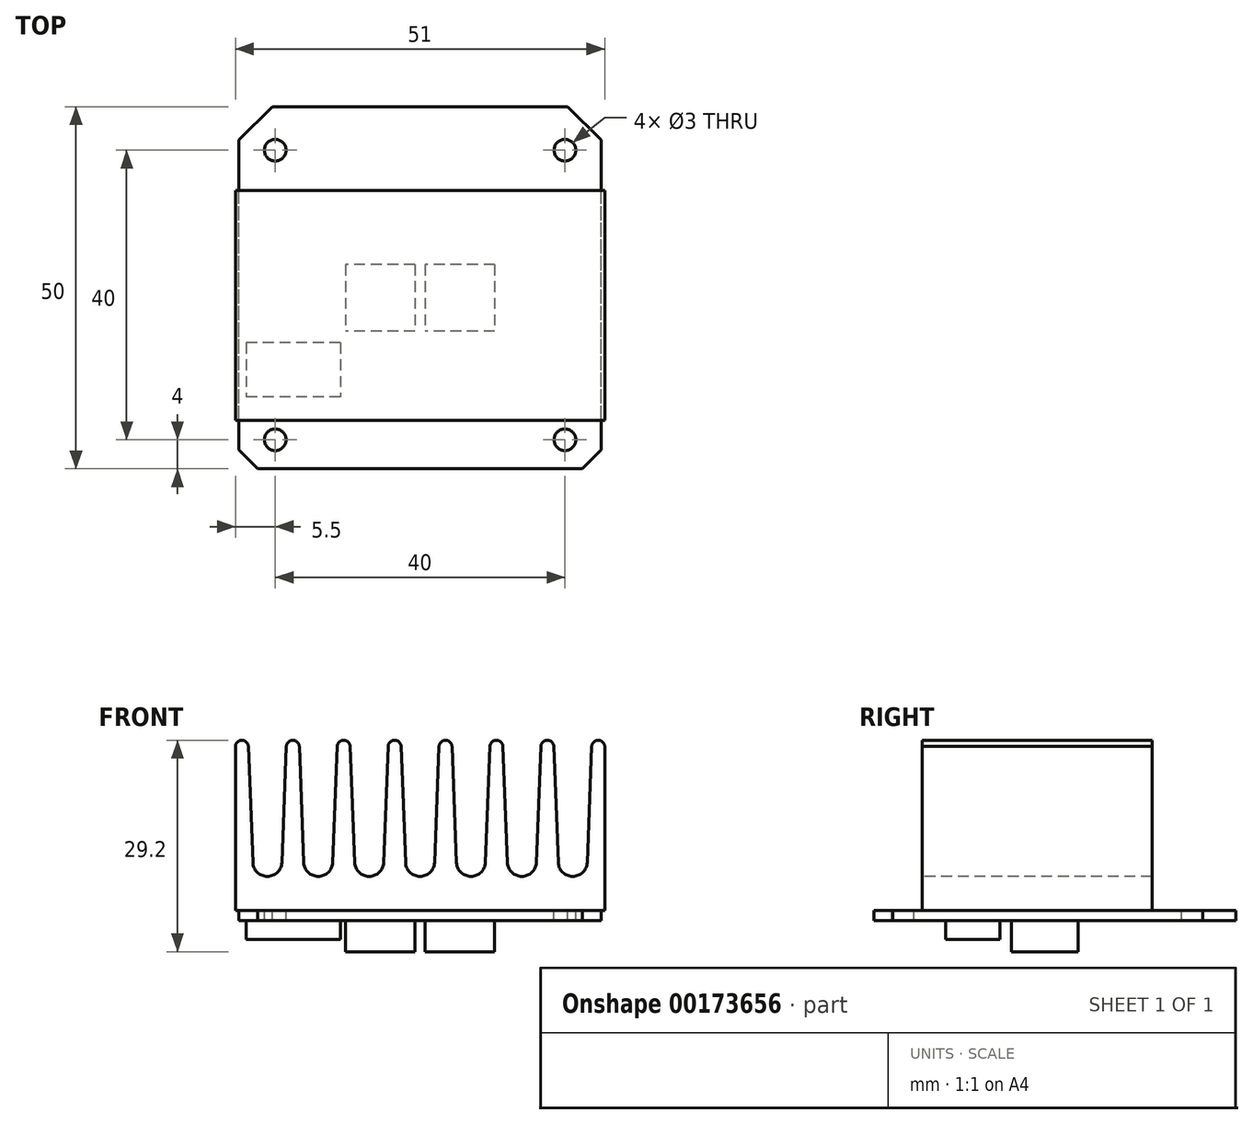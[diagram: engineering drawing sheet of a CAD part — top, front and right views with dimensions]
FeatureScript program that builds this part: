
annotation { "Feature Type Name" : "Feature", "Feature Type Description" : "" }
export const myFeature = defineFeature(function(context is Context, id is Id, definition is map)
    precondition{}
    {
        {
            var Q0;
            Q0=qCreatedBy(makeId("Top.planeOp"),FACE);
            var sketch = newSketch(context, id + "F0", { "sketchPlane" : qUnion([Q0])});
            skLineSegment(sketch, "E0.bottom", {"start": v(-25, -25) * mm, "end": v(25, -25) * mm});
            skLineSegment(sketch, "E0.top", {"start": v(-25, 25) * mm, "end": v(25, 25) * mm});
            skLineSegment(sketch, "E0.left", {"start": v(-25, -25) * mm, "end": v(-25, 25) * mm});
            skLineSegment(sketch, "E0.right", {"start": v(25, -25) * mm, "end": v(25, 25) * mm});
            skPoint(sketch, "E0.middle", {"position": v(0, 0) * mm});
            skLineSegment(sketch, "E1", {"start": v(0, 0) * mm, "end": v(0, -1) * mm, "construction": true});
            skLineSegment(sketch, "E2.bottom", {"start": v(20, 19) * mm, "end": v(-20, 19) * mm, "construction": true});
            skLineSegment(sketch, "E2.top", {"start": v(20, -21) * mm, "end": v(-20, -21) * mm, "construction": true});
            skLineSegment(sketch, "E2.left", {"start": v(20, 19) * mm, "end": v(20, -21) * mm, "construction": true});
            skLineSegment(sketch, "E2.right", {"start": v(-20, 19) * mm, "end": v(-20, -21) * mm, "construction": true});
            skPoint(sketch, "E2.middle", {"position": v(0, -1) * mm});
            skCircle(sketch, "E3", {"center": v(20, 19) * mm, "radius": 1.5 * mm});
            skCircle(sketch, "E4", {"center": v(20, -21) * mm, "radius": 1.5 * mm});
            skCircle(sketch, "E5", {"center": v(-20, -21) * mm, "radius": 1.5 * mm});
            skCircle(sketch, "E6", {"center": v(-20, 19) * mm, "radius": 1.5 * mm});
            skPoint(sketch, "E7.endSnap0", {"position": v(0, 19) * mm});
            skLineSegment(sketch, "E8", {"start": v(-12.7, 20.27) * mm, "end": v(2.54, 20.27) * mm, "construction": true});
            skPoint(sketch, "E9", {"position": v(-12.7, 20.27) * mm});
            skPoint(sketch, "E10", {"position": v(2.54, 20.27) * mm});
            skLineSegment(sketch, "E11", {"start": v(-25, -22.4) * mm, "end": v(-22.4, -25) * mm});
            skLineSegment(sketch, "E12", {"start": v(22.4, -25) * mm, "end": v(25, -22.4) * mm});
            skLineSegment(sketch, "E13", {"start": v(25, 20.4) * mm, "end": v(20.4, 25) * mm});
            skLineSegment(sketch, "E14", {"start": v(-20.4, 25) * mm, "end": v(-25, 20.4) * mm});
            skSolve(sketch);
        }
        {
            var Q0;
            Q0=makeQuery(id+"F0.imprint","IMPRINT",FACE,{"disambiguationData":[TD([[makeQuery(id+"F0.imprint","IMPRINT",EDGE,{"derivedFrom":sQuery(id+"F0.wireOp",EDGE,"E3")}),-1.0]])]});
            extrude(context, id + "F1", {"entities" : qUnion([Q0]), "oppositeDirection" : true, "depth" : 1.4 * mm});
        }
        {
            var Q0;
            Q0=makeQuery(id+"F0.imprint","IMPRINT",FACE,{"disambiguationData":[TD([[makeQuery(id+"F0.imprint","IMPRINT",EDGE,{"derivedFrom":sQuery(id+"F0.wireOp",EDGE,"E0.bottom")}),1.0]])]});
            var sketch = newSketch(context, id + "F2", { "sketchPlane" : qUnion([Q0])});
            skLineSegment(sketch, "E15.bottom", {"start": v(-25.5, 13.4) * mm, "end": v(25.5, 13.4) * mm});
            skLineSegment(sketch, "E15.top", {"start": v(-25.5, -18.3) * mm, "end": v(25.5, -18.3) * mm});
            skLineSegment(sketch, "E15.left", {"start": v(-25.5, 13.4) * mm, "end": v(-25.5, -18.3) * mm});
            skLineSegment(sketch, "E15.right", {"start": v(25.5, 13.4) * mm, "end": v(25.5, -18.3) * mm});
            skPoint(sketch, "E15.middle", {"position": v(0, -2.45) * mm});
            skSolve(sketch);
        }
        {
            var Q0;
            Q0 = qSketchRegion(id + "F2", true);
            extrude(context, id + "F3", {"entities" : qUnion([Q0]), "depth" : 23.5 * mm});
        }
        {
            var Q0;
            Q0=makeQuery(id+"F3.opExtrude","SWEPT_FACE",FACE,{"disambiguationData":[OSD([sQuery(id+"F2.wireOp",EDGE,"E15.top")])]});
            var sketch = newSketch(context, id + "F4", { "sketchPlane" : qUnion([Q0])});
            skLineSegment(sketch, "E16", {"start": v(-2.62, 22.63) * mm, "end": v(-2, 6.62) * mm});
            skArc(sketch, "E17", {"start": v(-2, 6.62) * mm, "mid": v(0, 4.7) * mm, "end": v(2, 6.62) * mm});
            skLineSegment(sketch, "E18", {"start": v(2, 6.62) * mm, "end": v(2.62, 22.63) * mm});
            skLineSegment(sketch, "E19", {"start": v(0, 23.5) * mm, "end": v(0, 6.7) * mm, "construction": true});
            skArc(sketch, "E20", {"start": v(4.41, 22.63) * mm, "mid": v(3.51, 23.5) * mm, "end": v(2.62, 22.63) * mm});
            skLineSegment(sketch, "E21.1.0.0", {"start": v(4.41, 22.63) * mm, "end": v(5.03, 6.62) * mm});
            skLineSegment(sketch, "E21.1.0.1", {"start": v(9.03, 6.62) * mm, "end": v(9.64, 22.63) * mm});
            skArc(sketch, "E21.1.0.2", {"start": v(11.44, 22.63) * mm, "mid": v(10.54, 23.5) * mm, "end": v(9.64, 22.63) * mm});
            skArc(sketch, "E21.1.0.3", {"start": v(5.03, 6.62) * mm, "mid": v(7.03, 4.7) * mm, "end": v(9.03, 6.62) * mm});
            skLineSegment(sketch, "E21.2.0.0", {"start": v(11.44, 22.63) * mm, "end": v(12.06, 6.62) * mm});
            skLineSegment(sketch, "E21.2.0.1", {"start": v(16.06, 6.62) * mm, "end": v(16.67, 22.63) * mm});
            skArc(sketch, "E21.2.0.2", {"start": v(18.47, 22.63) * mm, "mid": v(17.57, 23.5) * mm, "end": v(16.67, 22.63) * mm});
            skArc(sketch, "E21.2.0.3", {"start": v(12.06, 6.62) * mm, "mid": v(14.06, 4.7) * mm, "end": v(16.06, 6.62) * mm});
            skLineSegment(sketch, "E21.3.0.0", {"start": v(18.47, 22.63) * mm, "end": v(19.09, 6.62) * mm});
            skLineSegment(sketch, "E21.3.0.1", {"start": v(23.08, 6.62) * mm, "end": v(23.7, 22.63) * mm});
            skArc(sketch, "E21.3.0.3", {"start": v(19.09, 6.62) * mm, "mid": v(21.09, 4.7) * mm, "end": v(23.08, 6.62) * mm});
            skLineSegment(sketch, "E21.direction1", {"start": v(-2, 6.62) * mm, "end": v(5.03, 6.62) * mm, "construction": true});
            skArc(sketch, "E22", {"start": v(25.5, 22.63) * mm, "mid": v(24.6, 23.5) * mm, "end": v(23.7, 22.63) * mm});
            skArc(sketch, "E23.MirrorCS", {"start": v(-4.41, 22.63) * mm, "mid": v(-3.51, 23.5) * mm, "end": v(-2.62, 22.63) * mm});
            skLineSegment(sketch, "E24.MirrorCS", {"start": v(-4.41, 22.63) * mm, "end": v(-5.03, 6.62) * mm});
            skArc(sketch, "E25.MirrorCS", {"start": v(-5.03, 6.62) * mm, "mid": v(-7.03, 4.7) * mm, "end": v(-9.03, 6.62) * mm});
            skLineSegment(sketch, "E26.MirrorCS", {"start": v(-9.03, 6.62) * mm, "end": v(-9.64, 22.63) * mm});
            skArc(sketch, "E27.MirrorCS", {"start": v(-11.44, 22.63) * mm, "mid": v(-10.54, 23.5) * mm, "end": v(-9.64, 22.63) * mm});
            skLineSegment(sketch, "E28.MirrorCS", {"start": v(-11.44, 22.63) * mm, "end": v(-12.06, 6.62) * mm});
            skArc(sketch, "E29.MirrorCS", {"start": v(-12.06, 6.62) * mm, "mid": v(-14.06, 4.7) * mm, "end": v(-16.06, 6.62) * mm});
            skLineSegment(sketch, "E30.MirrorCS", {"start": v(-16.06, 6.62) * mm, "end": v(-16.67, 22.63) * mm});
            skArc(sketch, "E31.MirrorCS", {"start": v(-18.47, 22.63) * mm, "mid": v(-17.57, 23.5) * mm, "end": v(-16.67, 22.63) * mm});
            skLineSegment(sketch, "E32.MirrorCS", {"start": v(-18.47, 22.63) * mm, "end": v(-19.09, 6.62) * mm});
            skArc(sketch, "E33.MirrorCS", {"start": v(-19.09, 6.62) * mm, "mid": v(-21.09, 4.7) * mm, "end": v(-23.08, 6.62) * mm});
            skLineSegment(sketch, "E34.MirrorCS", {"start": v(-23.08, 6.62) * mm, "end": v(-23.7, 22.63) * mm});
            skArc(sketch, "E35", {"start": v(-23.7, 22.63) * mm, "mid": v(-24.6, 23.5) * mm, "end": v(-25.5, 22.63) * mm});
            skSolve(sketch);
        }
        {
            var Q0;
            {var subQ1=sQuery(id+"F4.wireOp",EDGE,"E32.MirrorCS");Q0=makeQuery(id+"F4.imprint","IMPRINT",FACE,{"disambiguationData":[TD([[makeQuery(id+"F4.imprint","IMPRINT",EDGE,{"derivedFrom":subQ1}),-1.0]])]});}
            var Q1;
            {var subQ0=sQuery(id+"F4.wireOp",EDGE,"E28.MirrorCS");Q1=makeQuery(id+"F4.imprint","IMPRINT",FACE,{"disambiguationData":[TD([[makeQuery(id+"F4.imprint","IMPRINT",EDGE,{"derivedFrom":subQ0}),-1.0]])]});}
            var Q2;
            {var subQ1=sQuery(id+"F4.wireOp",EDGE,"E24.MirrorCS");Q2=makeQuery(id+"F4.imprint","IMPRINT",FACE,{"disambiguationData":[TD([[makeQuery(id+"F4.imprint","IMPRINT",EDGE,{"derivedFrom":subQ1}),-1.0]])]});}
            var Q3;
            {var subQ6=sQuery(id+"F4.wireOp",EDGE,"E16");Q3=makeQuery(id+"F4.imprint","IMPRINT",FACE,{"disambiguationData":[TD([[makeQuery(id+"F4.imprint","IMPRINT",EDGE,{"derivedFrom":subQ6}),1.0]])]});}
            var Q4;
            {var subQ4=sQuery(id+"F4.wireOp",EDGE,"E21.1.0.0");Q4=makeQuery(id+"F4.imprint","IMPRINT",FACE,{"disambiguationData":[TD([[makeQuery(id+"F4.imprint","IMPRINT",EDGE,{"derivedFrom":subQ4}),1.0]])]});}
            var Q5;
            {var subQ6=sQuery(id+"F4.wireOp",EDGE,"E21.2.0.0");Q5=makeQuery(id+"F4.imprint","IMPRINT",FACE,{"disambiguationData":[TD([[makeQuery(id+"F4.imprint","IMPRINT",EDGE,{"derivedFrom":subQ6}),1.0]])]});}
            var Q6;
            {var subQ1=sQuery(id+"F4.wireOp",EDGE,"E21.3.0.0");Q6=makeQuery(id+"F4.imprint","IMPRINT",FACE,{"disambiguationData":[TD([[makeQuery(id+"F4.imprint","IMPRINT",EDGE,{"derivedFrom":subQ1}),1.0]])]});}
            var Q7;
            {var subQ0=sQuery(id+"F4.wireOp",EDGE,"E22");var subQ1=sQuery(id+"F2.wireOp",EDGE,"E15.top");var subQ4=makeQuery(id+"F3.opExtrude","CAP_EDGE",EDGE,{"disambiguationData":[OSD([subQ1])],"isStart":false});var subQ5=makeQuery(id+"F4.imprint","INTERSECT",VERTEX,{"derivedFrom":[subQ4,subQ0]});Q7=makeQuery(id+"F4.imprint","IMPRINT",FACE,{"disambiguationData":[TD([[makeQuery(id+"F4.imprint","IMPRINT",EDGE,{"disambiguationData":[TD([[subQ5,1.0]])],"derivedFrom":subQ0}),-1.0]])]});}
            var Q8;
            {var subQ0=sQuery(id+"F4.wireOp",EDGE,"E35");var subQ1=sQuery(id+"F2.wireOp",EDGE,"E15.top");var subQ4=makeQuery(id+"F3.opExtrude","CAP_EDGE",EDGE,{"disambiguationData":[OSD([subQ1])],"isStart":false});var subQ5=makeQuery(id+"F4.imprint","INTERSECT",VERTEX,{"derivedFrom":[subQ4,subQ0]});Q8=makeQuery(id+"F4.imprint","IMPRINT",FACE,{"disambiguationData":[TD([[makeQuery(id+"F4.imprint","IMPRINT",EDGE,{"disambiguationData":[TD([[subQ5,-1.0]])],"derivedFrom":subQ0}),-1.0]])]});}
            extrude(context, id + "F5", {"entities" : qUnion([Q0, Q1, Q2, Q3, Q4, Q5, Q6, Q7, Q8]), "operationType" : NewBodyOperationType.REMOVE, "endBound" : BoundingType.UP_TO_NEXT, "oppositeDirection" : true, "depth" : 25 * mm});
        }
        {
            var Q0;
            Q0=makeQuery(id+"F1.opExtrude","CAP_FACE",FACE,{"disambiguationData":[OSD([sQuery(id+"F0.wireOp",EDGE,"E0.bottom"),sQuery(id+"F0.wireOp",EDGE,"E0.top"),sQuery(id+"F0.wireOp",EDGE,"E0.left"),sQuery(id+"F0.wireOp",EDGE,"E0.right"),sQuery(id+"F0.wireOp",EDGE,"E3"),sQuery(id+"F0.wireOp",EDGE,"E4"),sQuery(id+"F0.wireOp",EDGE,"E5"),sQuery(id+"F0.wireOp",EDGE,"E6")])],"isStart":false});
            var sketch = newSketch(context, id + "F6", { "sketchPlane" : qUnion([Q0])});
            skLineSegment(sketch, "E36.bottom", {"start": v(10.3, -3.2) * mm, "end": v(0.7, -3.2) * mm});
            skLineSegment(sketch, "E36.top", {"start": v(10.3, 6) * mm, "end": v(0.7, 6) * mm});
            skLineSegment(sketch, "E36.left", {"start": v(10.3, -3.2) * mm, "end": v(10.3, 6) * mm});
            skLineSegment(sketch, "E36.right", {"start": v(0.7, -3.2) * mm, "end": v(0.7, 6) * mm});
            skLineSegment(sketch, "E37.bottom", {"start": v(-0.7, -3.2) * mm, "end": v(-10.3, -3.2) * mm});
            skLineSegment(sketch, "E37.top", {"start": v(-0.7, 6) * mm, "end": v(-10.3, 6) * mm});
            skLineSegment(sketch, "E37.left", {"start": v(-0.7, -3.2) * mm, "end": v(-0.7, 6) * mm});
            skLineSegment(sketch, "E37.right", {"start": v(-10.3, -3.2) * mm, "end": v(-10.3, 6) * mm});
            skLineSegment(sketch, "E38.bottom", {"start": v(-11, 7.6) * mm, "end": v(-24, 7.6) * mm});
            skLineSegment(sketch, "E38.top", {"start": v(-11, 15.1) * mm, "end": v(-24, 15.1) * mm});
            skLineSegment(sketch, "E38.left", {"start": v(-11, 7.6) * mm, "end": v(-11, 15.1) * mm});
            skLineSegment(sketch, "E38.right", {"start": v(-24, 7.6) * mm, "end": v(-24, 15.1) * mm});
            skLineSegment(sketch, "E39", {"start": v(0.7, 0) * mm, "end": v(-0.7, 0) * mm, "construction": true});
            skSolve(sketch);
        }
        {
            var Q0;
            Q0=makeQuery(id+"F6.imprint","IMPRINT",FACE,{"disambiguationData":[TD([[makeQuery(id+"F6.imprint","IMPRINT",EDGE,{"derivedFrom":sQuery(id+"F6.wireOp",EDGE,"E36.bottom")}),-1.0]])]});
            var Q1;
            Q1=makeQuery(id+"F6.imprint","IMPRINT",FACE,{"disambiguationData":[TD([[makeQuery(id+"F6.imprint","IMPRINT",EDGE,{"derivedFrom":sQuery(id+"F6.wireOp",EDGE,"E37.bottom")}),-1.0]])]});
            extrude(context, id + "F7", {"entities" : qUnion([Q0, Q1]), "depth" : 4.3 * mm});
        }
        {
            var Q0;
            Q0=makeQuery(id+"F6.imprint","IMPRINT",FACE,{"disambiguationData":[TD([[makeQuery(id+"F6.imprint","IMPRINT",EDGE,{"derivedFrom":sQuery(id+"F6.wireOp",EDGE,"E38.bottom")}),-1.0]])]});
            extrude(context, id + "F8", {"entities" : qUnion([Q0]), "depth" : 2.6 * mm});
        }
    });
